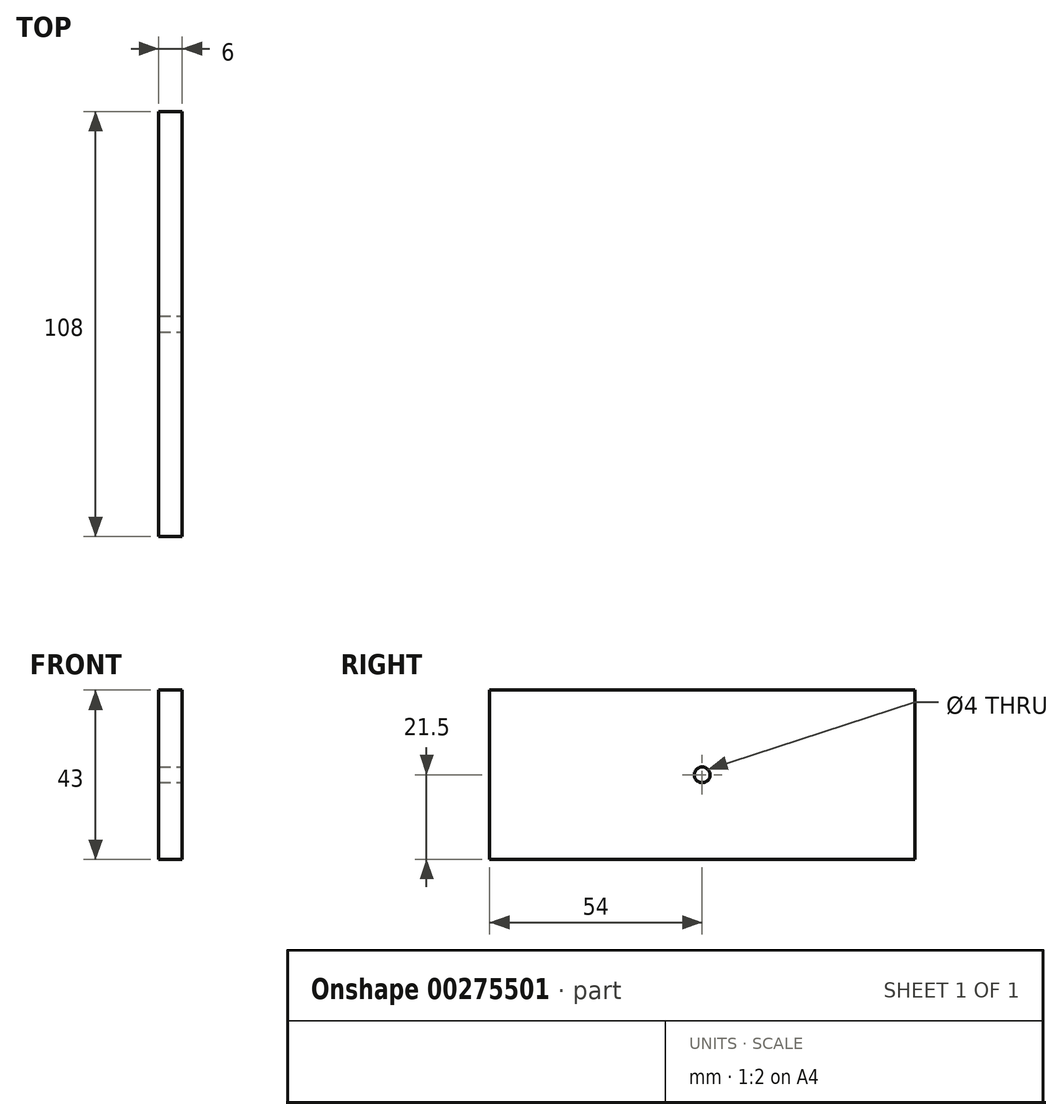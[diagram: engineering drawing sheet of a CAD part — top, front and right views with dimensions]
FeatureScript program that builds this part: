
annotation { "Feature Type Name" : "Feature", "Feature Type Description" : "" }
export const myFeature = defineFeature(function(context is Context, id is Id, definition is map)
    precondition{}
    {
        {
            var Q0;
            Q0=qCreatedBy(makeId("Right.planeOp"),FACE);
            var sketch = newSketch(context, id + "F0", { "sketchPlane" : qUnion([Q0])});
            skLineSegment(sketch, "E0.bottom", {"start": v(0, 0) * mm, "end": v(108, 0) * mm});
            skLineSegment(sketch, "E0.top", {"start": v(0, 43) * mm, "end": v(108, 43) * mm});
            skLineSegment(sketch, "E0.left", {"start": v(0, 0) * mm, "end": v(0, 43) * mm});
            skLineSegment(sketch, "E0.right", {"start": v(108, 0) * mm, "end": v(108, 43) * mm});
            skSolve(sketch);
        }
        {
            var Q0;
            Q0=makeQuery(id+"F0.imprint","IMPRINT",FACE,{"disambiguationData":[TD([[makeQuery(id+"F0.imprint","IMPRINT",EDGE,{"derivedFrom":sQuery(id+"F0.wireOp",EDGE,"E0.bottom")}),1.0]])]});
            extrude(context, id + "F1", {"entities" : qUnion([Q0]), "depth" : 6 * mm});
        }
        {
            var Q0;
            Q0=makeQuery(id+"F1.opExtrude","CAP_FACE",FACE,{"disambiguationData":[OSD([sQuery(id+"F0.wireOp",EDGE,"E0.bottom"),sQuery(id+"F0.wireOp",EDGE,"E0.top"),sQuery(id+"F0.wireOp",EDGE,"E0.left"),sQuery(id+"F0.wireOp",EDGE,"E0.right")])],"isStart":false});
            var sketch = newSketch(context, id + "F2", { "sketchPlane" : qUnion([Q0])});
            skPoint(sketch, "E1", {"position": v(54, 21.5) * mm});
            skPoint(sketch, "E1.positionSnap0", {"position": v(0, 21.5) * mm});
            skPoint(sketch, "E1.positionSnap1", {"position": v(54, 43) * mm});
            skSolve(sketch);
        }
        {
            var Q0;
            Q0=sQuery(id+"F2.wireOp",VERTEX,"E1");
            var Q1;
            Q1=makeQuery(id+"F1.opExtrude","SWEPT_BODY",BODY,{"disambiguationData":[OSD([sQuery(id+"F0.wireOp",EDGE,"E0.bottom"),sQuery(id+"F0.wireOp",EDGE,"E0.top"),sQuery(id+"F0.wireOp",EDGE,"E0.left"),sQuery(id+"F0.wireOp",EDGE,"E0.right")])]});
            hole(context, id + "F3", {"style" : HoleStyle.SIMPLE, "endStyle" : HoleEndStyle.THROUGH, "holeDiameter" : 4 * mm, "tappedDepth" : 12 * mm, "tapClearance" : 3, "locations" : qUnion([Q0]), "scope" : qUnion([Q1])});
        }
    });
